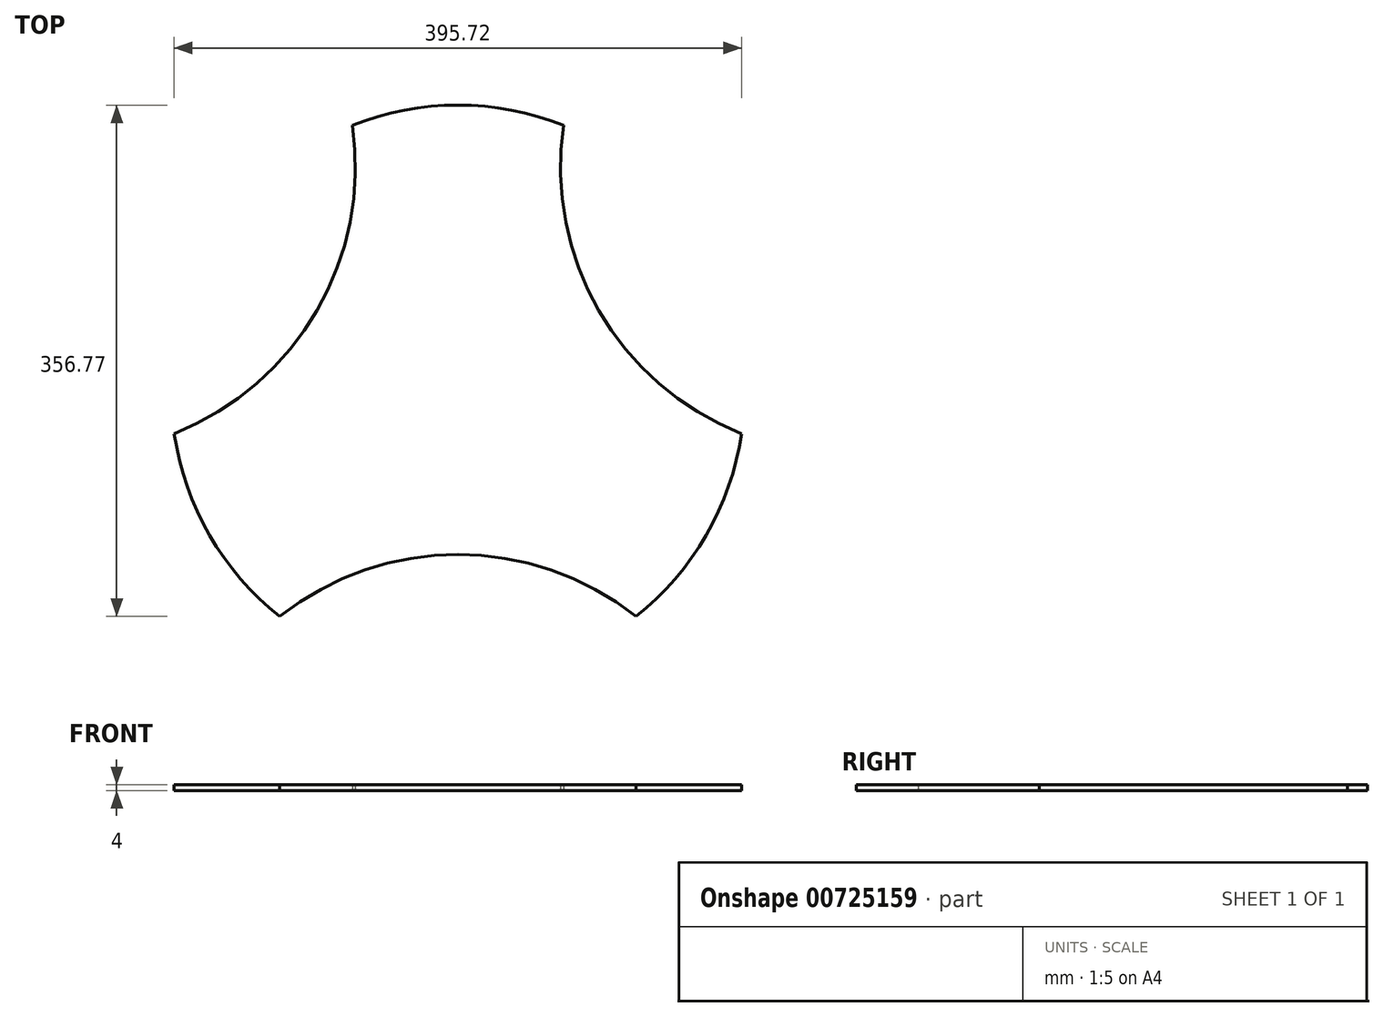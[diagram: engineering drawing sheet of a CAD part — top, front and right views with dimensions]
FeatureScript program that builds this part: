
annotation { "Feature Type Name" : "Feature", "Feature Type Description" : "" }
export const myFeature = defineFeature(function(context is Context, id is Id, definition is map)
    precondition{}
    {
        {
            var Q0;
            Q0=qCreatedBy(makeId("Top.planeOp"),FACE);
            var sketch = newSketch(context, id + "F0", { "sketchPlane" : qUnion([Q0])});
            skArc(sketch, "E0", {"start": v(73.67, 185.94) * mm, "mid": v(0, 200) * mm, "end": v(-73.67, 185.94) * mm});
            skLineSegment(sketch, "E1.0", {"start": v(0, 200) * mm, "end": v(173.2, -100) * mm, "construction": true});
            skLineSegment(sketch, "E1.1", {"start": v(173.2, -100) * mm, "end": v(-173.2, -100) * mm, "construction": true});
            skLineSegment(sketch, "E1.2", {"start": v(-173.2, -100) * mm, "end": v(0, 200) * mm, "construction": true});
            skLineSegment(sketch, "E2", {"start": v(0, 200) * mm, "end": v(73.67, 185.94) * mm, "construction": true});
            skLineSegment(sketch, "E3", {"start": v(0, 200) * mm, "end": v(-73.67, 185.94) * mm, "construction": true});
            skArc(sketch, "E4", {"start": v(73.67, 185.94) * mm, "mid": v(98.33, 56.77) * mm, "end": v(197.86, -29.17) * mm});
            skArc(sketch, "E5.1.0", {"start": v(124.2, -156.77) * mm, "mid": v(173.2, -100) * mm, "end": v(197.86, -29.17) * mm});
            skArc(sketch, "E5.2.0", {"start": v(-197.86, -29.17) * mm, "mid": v(-173.2, -100) * mm, "end": v(-124.2, -156.77) * mm});
            skLineSegment(sketch, "E5.anchor1", {"start": v(0, 0) * mm, "end": v(-73.67, 185.94) * mm, "construction": true});
            skLineSegment(sketch, "E5.anchor2", {"start": v(0, 0) * mm, "end": v(-124.2, -156.77) * mm, "construction": true});
            skArc(sketch, "E6.1.0", {"start": v(-197.86, -29.17) * mm, "mid": v(-98.33, 56.77) * mm, "end": v(-73.67, 185.94) * mm});
            skArc(sketch, "E6.2.0", {"start": v(124.2, -156.77) * mm, "mid": v(0, -113.54) * mm, "end": v(-124.2, -156.77) * mm});
            skSolve(sketch);
        }
        {
            var Q0;
            Q0 = qSketchRegion(id + "F0", true);
            extrude(context, id + "F1", {"entities" : qUnion([Q0]), "depth" : 4 * mm, "offsetDistance" : 25 * mm});
        }
    });
